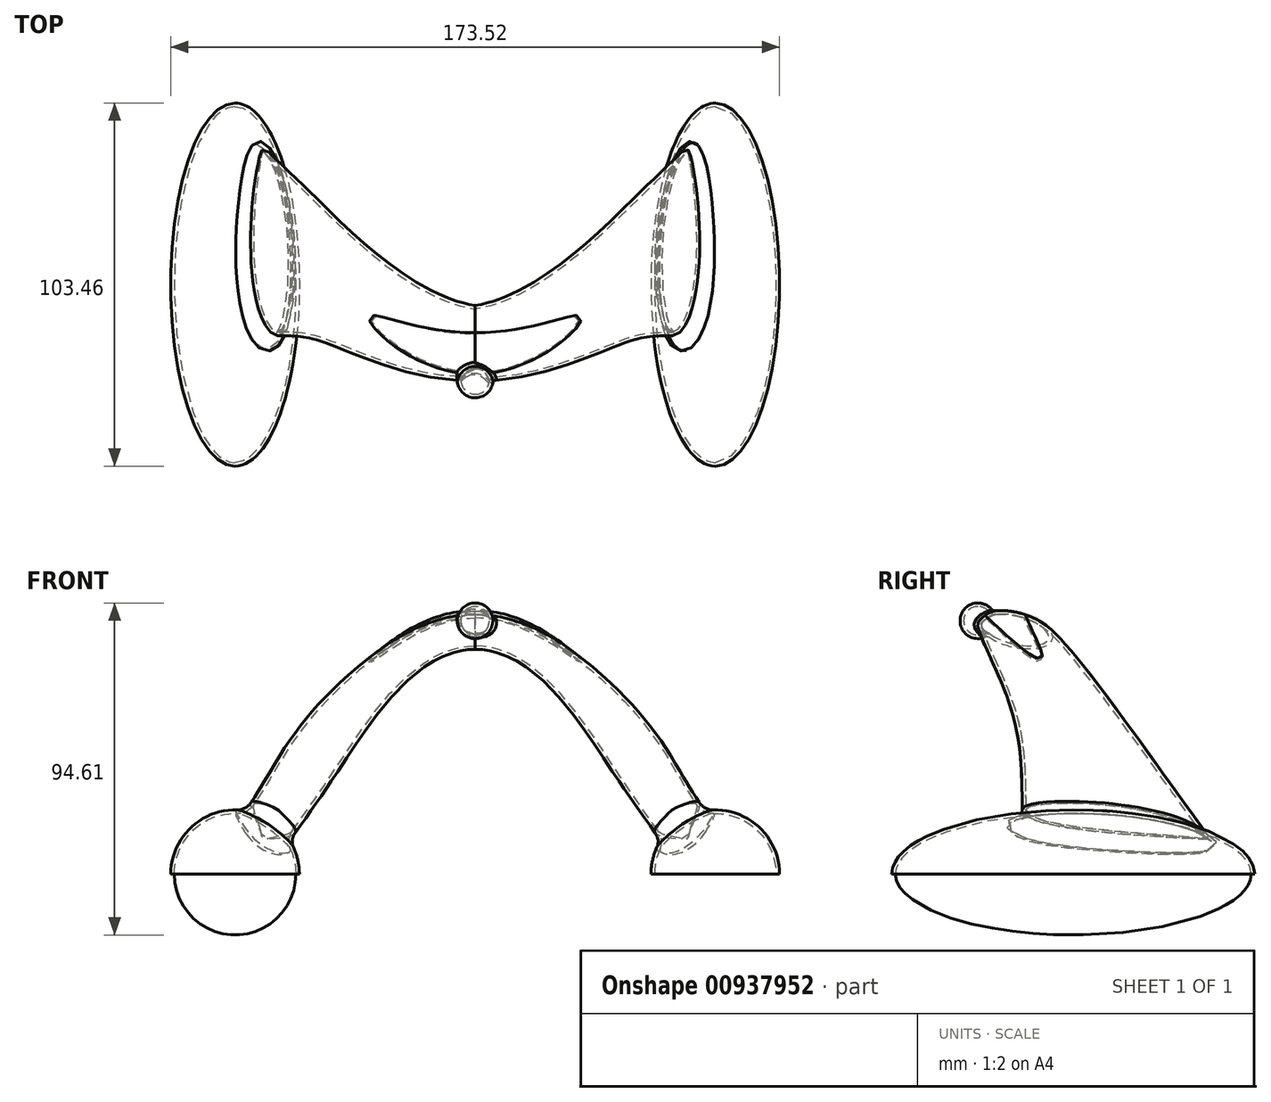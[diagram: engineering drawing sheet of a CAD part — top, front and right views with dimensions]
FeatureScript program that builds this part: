
annotation { "Feature Type Name" : "Feature", "Feature Type Description" : "" }
export const myFeature = defineFeature(function(context is Context, id is Id, definition is map)
    precondition{}
    {
        {
            var Q0;
            Q0=qCreatedBy(makeId("Top.planeOp"),FACE);
            var sketch = newSketch(context, id + "F0", { "sketchPlane" : qUnion([Q0])});
            skLineSegment(sketch, "E0", {"start": v(0, 0) * mm, "end": v(0, 66.09) * mm, "construction": true});
            skEllipticalArc(sketch, "E1", {});
            skLineSegment(sketch, "E2", {"start": v(-68.43, 0) * mm, "end": v(-68.43, 65.2) * mm, "construction": true});
            skLineSegment(sketch, "E3", {"start": v(-68.43, 51.73) * mm, "end": v(-68.43, -51.73) * mm});
            const initialGuessF0  = {"E1": [-0.06843346357345581, 0, 0, 1, 0.05172807723283768, 0.018322502828257106, 0, 3.141592653589793]};
            skSetInitialGuess(sketch, initialGuessF0);
            skSolve(sketch);
        }
        {
            var Q0;
            Q0 = qSketchRegion(id + "F0", true);
            var Q1;
            Q1=sQuery(id+"F0.wireOp",EDGE,"E2");
            revolve(context, id + "F1", {"surfaceOperationType" : NewSurfaceOperationType.NEW, "entities" : qUnion([Q0]), "axis" : qUnion([Q1]), "revolveType" : RevolveType.ONE_DIRECTION, "angle" : 180 * degree});
        }
        {
            var Q0;
            Q0=makeQuery(id+"F1.opRevolve","CAP_FACE",FACE,{"disambiguationData":[OSD([sQuery(id+"F0.wireOp",EDGE,"E1"),sQuery(id+"F0.wireOp",EDGE,"E3")])],"isStart":false});
            var sketch = newSketch(context, id + "F2", { "sketchPlane" : qUnion([Q0])});
            skEllipse(sketch, "E4", {"center": v(-69.02, -15.68) * mm, "majorRadius": 30.77 * mm, "minorRadius": 9.23 * mm, "majorAxis": v(0, 1)});
            skPoint(sketch, "E5", {"position": v(-69.02, -46.45) * mm});
            skSolve(sketch);
        }
        {
            var Q0;
            Q0=qCreatedBy(makeId("Right.planeOp"),FACE);
            var sketch = newSketch(context, id + "F3", { "sketchPlane" : qUnion([Q0])});
            skEllipse(sketch, "E6", {"center": v(-16.56, 69.6) * mm, "majorRadius": 10.88 * mm, "minorRadius": 4.98 * mm, "majorAxis": v(0.97, -0.24)});
            skPoint(sketch, "E7", {"position": v(-6, 66.97) * mm});
            skSolve(sketch);
        }
        {
            var Q0;
            Q0=qCreatedBy(makeId("Top.planeOp"),FACE);
            var sketch = newSketch(context, id + "F4", { "sketchPlane" : qUnion([Q0])});
            skLineSegment(sketch, "E8", {"start": v(0, 0) * mm, "end": v(0, 53.78) * mm, "construction": true});
            skEllipse(sketch, "E9.0", {"center": v(-69.02, 15.68) * mm, "majorRadius": 30.77 * mm, "minorRadius": 9.23 * mm, "majorAxis": v(0, -1), "construction": true});
            skEllipse(sketch, "E10.MirrorC", {"center": v(69.02, 15.68) * mm, "majorRadius": 30.77 * mm, "minorRadius": 9.23 * mm, "majorAxis": v(0, -1)});
            skPoint(sketch, "E11", {"position": v(69.02, 46.45) * mm});
            skSolve(sketch);
        }
        {
            var Q0;
            Q0=sQuery(id+"F2.wireOp",VERTEX,"E5");
            var Q1;
            Q1=sQuery(id+"F3.wireOp",VERTEX,"E7");
            var Q2;
            Q2=sQuery(id+"F4.wireOp",VERTEX,"E11");
            cPlane(context, id + "F5", {"entities" : qUnion([Q0, Q1, Q2]), "cplaneType" : CPlaneType.THREE_POINT, "offset" : 25.4 * mm, "width" : 152.4 * mm, "height" : 152.4 * mm});
        }
        {
            var Q0;
            Q0=qCreatedBy(id+"F5.planeOp",FACE);
            var sketch = newSketch(context, id + "F6", { "sketchPlane" : qUnion([Q0])});
            skLineSegment(sketch, "E12", {"start": v(69.02, -28.65) * mm, "end": v(21.3, 44.85) * mm});
            skArc(sketch, "E13", {"start": v(21.3, 44.85) * mm, "mid": v(0, 56.42) * mm, "end": v(-21.3, 44.85) * mm});
            skLineSegment(sketch, "E14", {"start": v(-21.3, 44.85) * mm, "end": v(-69.02, -28.65) * mm});
            skLineSegment(sketch, "E15", {"start": v(0, 31.02) * mm, "end": v(0, -12.34) * mm, "construction": true});
            skSolve(sketch);
        }
        {
            var Q0;
            Q0=sQuery(id+"F6.wireOp",EDGE,"E14");
            var Q1;
            Q1=sQuery(id+"F6.wireOp",EDGE,"E13");
            var Q2;
            Q2=sQuery(id+"F6.wireOp",EDGE,"E12");
            var Q4;
            Q4 = qSketchRegion(id + "F2", true);
            var Q5;
            Q5 = qSketchRegion(id + "F3", true);
            var Q6;
            Q6 = qSketchRegion(id + "F4", true);
            loft(context, id + "F7", {"operationType" : NewBodyOperationType.ADD, "addSections" : true, "spine" : qUnion([Q0, Q1, Q2]), "sectionCount" : 5, "sheetProfilesArray" : [{ "sheetProfileEntities" : qUnion([Q4]) }, { "sheetProfileEntities" : qUnion([Q5]) }, { "sheetProfileEntities" : qUnion([Q6]) }]});
        }
        {
            var Q0;
            Q0=makeQuery(id+"F1.opRevolve","SWEPT_BODY",BODY,{"disambiguationData":[OSD([sQuery(id+"F0.wireOp",EDGE,"E1"),sQuery(id+"F0.wireOp",EDGE,"E3")])]});
            var Q1;
            Q1=qCreatedBy(makeId("Right.planeOp"),FACE);
            mirror(context, id + "F8", {"operationType" : NewBodyOperationType.ADD, "entities" : qUnion([Q0]), "mirrorPlane" : qUnion([Q1])});
        }
        {
            var Q0;
            Q0=makeQuery(id+"F8.boolean.opBoolean","INTERSECT",EDGE,{"derivedFrom":[makeQuery(id+"F1.opRevolve","SWEPT_FACE",FACE,{"disambiguationData":[OSD([sQuery(id+"F0.wireOp",EDGE,"E1")])]}),makeQuery(id+"F8.opPattern","COPY",FACE,{"derivedFrom":makeQuery(id+"F7.opLoft","SWEPT_FACE",FACE,{"disambiguationData":[OSD([sQuery(id+"F2.wireOp",EDGE,"E4"),sQuery(id+"F3.wireOp",EDGE,"E6"),sQuery(id+"F4.wireOp",EDGE,"E10.MirrorC")])]}),"instanceName":"1"})]});
            var Q1;
            Q1=makeQuery(id+"F8.boolean.opBoolean","INTERSECT",EDGE,{"derivedFrom":[makeQuery(id+"F7.opLoft","SWEPT_FACE",FACE,{"disambiguationData":[OSD([sQuery(id+"F2.wireOp",EDGE,"E4"),sQuery(id+"F3.wireOp",EDGE,"E6"),sQuery(id+"F4.wireOp",EDGE,"E10.MirrorC")])]}),makeQuery(id+"F8.opPattern","COPY",FACE,{"derivedFrom":makeQuery(id+"F1.opRevolve","SWEPT_FACE",FACE,{"disambiguationData":[OSD([sQuery(id+"F0.wireOp",EDGE,"E1")])]}),"instanceName":"1"})]});
            fillet(context, id + "F9", {"entities" : qUnion([Q0, Q1]), "radius" : 5.08 * mm, "tangentPropagation" : true, "allowEdgeOverflow" : false});
        }
        {
            var Q0;
            Q0=qCreatedBy(makeId("Right.planeOp"),FACE);
            var sketch = newSketch(context, id + "F10", { "sketchPlane" : qUnion([Q0])});
            skLineSegment(sketch, "E16", {"start": v(-27.18, 77.29) * mm, "end": v(-27.18, 63.78) * mm, "construction": true});
            skArc(sketch, "E17", {"start": v(-27.18, 77.29) * mm, "mid": v(-22.1, 72.2) * mm, "end": v(-27.18, 67.13) * mm});
            skLineSegment(sketch, "E18", {"start": v(-27.18, 67.13) * mm, "end": v(-27.18, 77.29) * mm});
            skSolve(sketch);
        }
        {
            var Q0;
            Q0 = qSketchRegion(id + "F10", true);
            var Q1;
            Q1=sQuery(id+"F10.wireOp",EDGE,"E16");
            revolve(context, id + "F11", {"operationType" : NewBodyOperationType.ADD, "surfaceOperationType" : NewSurfaceOperationType.NEW, "entities" : qUnion([Q0]), "axis" : qUnion([Q1]), "revolveType" : RevolveType.FULL});
        }
        {
            var Q0;
            {var subQ0=makeQuery(id+"F7.opLoft","SWEPT_FACE",FACE,{"disambiguationData":[OSD([sQuery(id+"F2.wireOp",EDGE,"E4"),sQuery(id+"F3.wireOp",EDGE,"E6"),sQuery(id+"F4.wireOp",EDGE,"E10.MirrorC")])]});var subQ1=subQ0;Q0=makeQuery(id+"F11.boolean.opBoolean","INTERSECT",EDGE,{"derivedFrom":[makeQuery(id+"F8.boolean.opBoolean","SPLIT",FACE,{"disambiguationData":[TD([subQ0,makeQuery(id+"F8.opPattern","COPY",FACE,{"derivedFrom":makeQuery(id+"F1.opRevolve","SWEPT_FACE",FACE,{"disambiguationData":[OSD([sQuery(id+"F0.wireOp",EDGE,"E1")])]}),"instanceName":"1"}),makeQuery(id+"F8.opPattern","COPY",FACE,{"derivedFrom":subQ1,"instanceName":"1"})])],"derivedFrom":subQ1}),makeQuery(id+"F11.opRevolve","SWEPT_FACE",FACE,{"disambiguationData":[OSD([sQuery(id+"F10.wireOp",EDGE,"E17")])]})]});}
            fillet(context, id + "F12", {"entities" : qUnion([Q0]), "radius" : 1.27 * mm, "tangentPropagation" : true, "allowEdgeOverflow" : false});
        }
        {
            var Q0;
            Q0=makeQuery(id+"F8.boolean.opBoolean","MERGE",FACE,{"derivedFrom":[makeQuery(id+"F7.opLoft","CAP_FACE",FACE,{"disambiguationData":[OSD([makeQuery(id+"F4.imprint","IMPRINT",FACE,{"disambiguationData":[TD([[makeQuery(id+"F4.imprint","IMPRINT",EDGE,{"derivedFrom":sQuery(id+"F4.wireOp",EDGE,"E10.MirrorC")}),1.0]])]})])],"isStart":true}),makeQuery(id+"F8.opPattern","COPY",FACE,{"derivedFrom":makeQuery(id+"F1.opRevolve","CAP_FACE",FACE,{"disambiguationData":[OSD([sQuery(id+"F0.wireOp",EDGE,"E1"),sQuery(id+"F0.wireOp",EDGE,"E3")])],"isStart":false}),"instanceName":"1"})]});
            var Q1;
            Q1=makeQuery(id+"F1.opRevolve","CAP_FACE",FACE,{"disambiguationData":[OSD([sQuery(id+"F0.wireOp",EDGE,"E1"),sQuery(id+"F0.wireOp",EDGE,"E3")])],"isStart":false});
            shell(context, id + "F13", {"entities" : qUnion([Q0, Q1]), "thickness" : 1 * mm});
        }
    });
